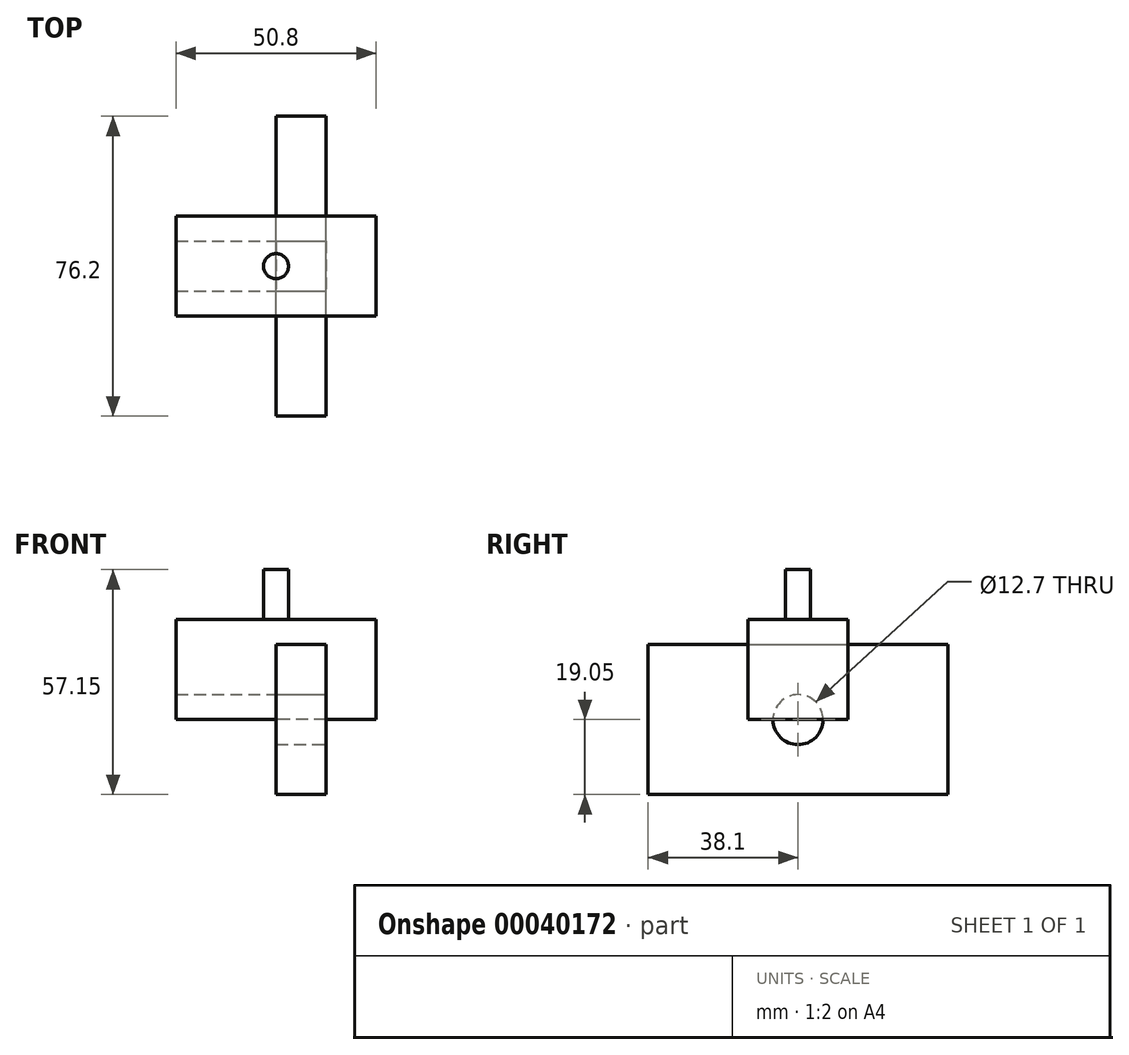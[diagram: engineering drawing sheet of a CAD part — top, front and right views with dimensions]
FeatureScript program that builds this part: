
annotation { "Feature Type Name" : "Feature", "Feature Type Description" : "" }
export const myFeature = defineFeature(function(context is Context, id is Id, definition is map)
    precondition{}
    {
        {
            var Q0;
            Q0=qCreatedBy(makeId("Top.planeOp"),FACE);
            var sketch = newSketch(context, id + "F0", { "sketchPlane" : qUnion([Q0])});
            skLineSegment(sketch, "E0.rect.bottom", {"start": v(25.4, 12.7) * mm, "end": v(-25.4, 12.7) * mm});
            skLineSegment(sketch, "E0.rect.top", {"start": v(25.4, -12.7) * mm, "end": v(-25.4, -12.7) * mm});
            skLineSegment(sketch, "E0.rect.left", {"start": v(25.4, 12.7) * mm, "end": v(25.4, -12.7) * mm});
            skLineSegment(sketch, "E0.rect.right", {"start": v(-25.4, 12.7) * mm, "end": v(-25.4, -12.7) * mm});
            skPoint(sketch, "E0.rect.middle", {"position": v(0, 0) * mm});
            skSolve(sketch);
        }
        {
            var Q0;
            Q0 = qSketchRegion(id + "F0", true);
            extrude(context, id + "F1", {"entities" : qUnion([Q0]), "depth" : 25.4 * mm});
        }
        {
            var Q0;
            Q0=makeQuery(id+"F1.opExtrude","CAP_FACE",FACE,{"disambiguationData":[OSD([sQuery(id+"F0.wireOp",EDGE,"E0.rect.bottom"),sQuery(id+"F0.wireOp",EDGE,"E0.rect.top"),sQuery(id+"F0.wireOp",EDGE,"E0.rect.left"),sQuery(id+"F0.wireOp",EDGE,"E0.rect.right")])],"isStart":false});
            var sketch = newSketch(context, id + "F2", { "sketchPlane" : qUnion([Q0])});
            skCircle(sketch, "E1", {"center": v(0, 0) * mm, "radius": 3.18 * mm});
            skSolve(sketch);
        }
        {
            var Q0;
            Q0 = qSketchRegion(id + "F2", true);
            extrude(context, id + "F3", {"entities" : qUnion([Q0]), "operationType" : NewBodyOperationType.ADD, "depth" : 12.7 * mm});
        }
        {
            var Q0;
            Q0=qCreatedBy(makeId("Right.planeOp"),FACE);
            var sketch = newSketch(context, id + "F4", { "sketchPlane" : qUnion([Q0])});
            skLineSegment(sketch, "E2.rect.bottom", {"start": v(-38.1, -19.05) * mm, "end": v(38.1, -19.05) * mm});
            skLineSegment(sketch, "E2.rect.top", {"start": v(-38.1, 19.05) * mm, "end": v(38.1, 19.05) * mm});
            skLineSegment(sketch, "E2.rect.left", {"start": v(-38.1, -19.05) * mm, "end": v(-38.1, 19.05) * mm});
            skLineSegment(sketch, "E2.rect.right", {"start": v(38.1, -19.05) * mm, "end": v(38.1, 19.05) * mm});
            skPoint(sketch, "E2.rect.middle", {"position": v(0, 0) * mm});
            skSolve(sketch);
        }
        {
            var Q0;
            Q0 = qSketchRegion(id + "F4", true);
            extrude(context, id + "F5", {"entities" : qUnion([Q0]), "depth" : 12.7 * mm});
        }
        {
            var Q0;
            Q0=makeQuery(id+"F5.opExtrude","CAP_FACE",FACE,{"disambiguationData":[OSD([sQuery(id+"F4.wireOp",EDGE,"E2.rect.bottom"),sQuery(id+"F4.wireOp",EDGE,"E2.rect.top"),sQuery(id+"F4.wireOp",EDGE,"E2.rect.left"),sQuery(id+"F4.wireOp",EDGE,"E2.rect.right")])],"isStart":false});
            var sketch = newSketch(context, id + "F6", { "sketchPlane" : qUnion([Q0])});
            skCircle(sketch, "E3", {"center": v(0, 0) * mm, "radius": 6.35 * mm});
            skSolve(sketch);
        }
        {
            var Q0;
            Q0 = qSketchRegion(id + "F6", true);
            extrude(context, id + "F7", {"entities" : qUnion([Q0]), "operationType" : NewBodyOperationType.REMOVE, "endBound" : BoundingType.THROUGH_ALL, "oppositeDirection" : true, "depth" : 25.4 * mm});
        }
    });
